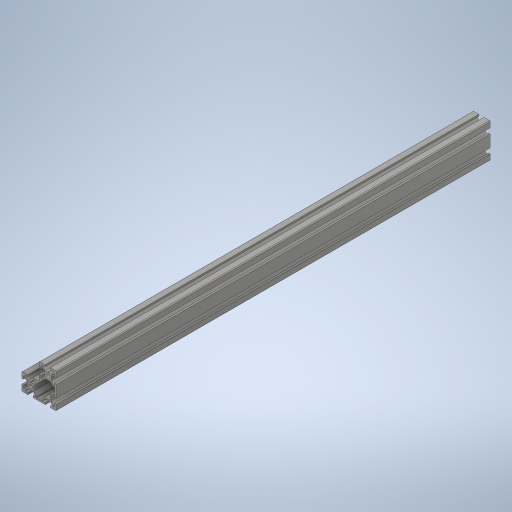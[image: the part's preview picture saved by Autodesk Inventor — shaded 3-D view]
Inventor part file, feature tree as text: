
AUTODESK INVENTOR PART (.ipt)
format: ipt  version: 2024 (Build 280153000, 153)  size: 445,952 bytes
history: native  units: mm
features: thread x4, sketch x3, hole x2, extrude x1
ambient origin geometry x8: Origin, YZ Plane, XZ Plane, XY Plane, X Axis, Y Axis, Z Axis, Center Point
bodies: Solid1 (feature_tree)
feature tree (10):
  extrude  "Extrusion1"  Depth=10.0mm TaperAngle=0.0deg
  hole  "Hole1"  [1 undecoded]
  hole  "Hole2"  [1 undecoded]
  thread  "Thread1"  [1 undecoded]
  thread  "Thread2"  [1 undecoded]
  thread  "Thread3"  [1 undecoded]
  thread  "Thread4"  [1 undecoded]
  sketch  "Sketch_1"  dims[d0=500.0mm d1=0.0mm]
  sketch  "Sketch2"  dims[d2=4.2mm d3=6.0mm d4=4.0mm d5=2.0mm d6=90.0deg d7=425.0mm d8=0.0mm]
  sketch  "Sketch3"  dims[d9=4.2mm d10=6.0mm d11=4.0mm d12=2.0mm d13=90.0deg d14=425.0mm d15=0.0mm d16=10.0mm d17=0.0mm d18=10.0mm d19=0.0mm d20=10.0mm d21=0.0mm d22=10.0mm d23=0.0mm]
note: 6 required parameter values undecoded (feature->parameter linkage not recoverable at this tier; creation-order binding heuristic only, values carry confidence <= 0.55)
